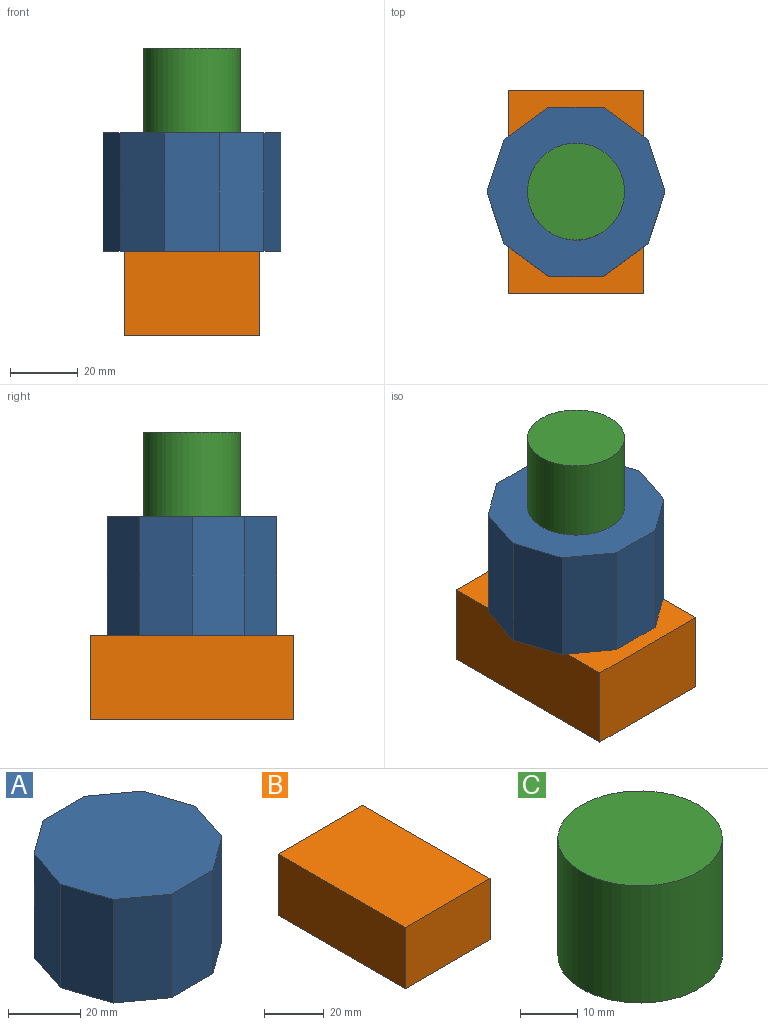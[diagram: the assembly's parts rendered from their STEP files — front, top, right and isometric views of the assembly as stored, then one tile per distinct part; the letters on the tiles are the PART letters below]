
ASSEMBLY  parts=3 mates=2
PART A: 12 faces, bbox 52.6x50x35 mm
  f0: plane 35x16.25mm, normal (0,1,0), area 568.6mm2, adj f1,f9,f10,f11
  f1: plane 35x13.14mm, normal (-0.59,0.81,0), area 568.6mm2, adj f0,f2,f10,f11
  f2: plane 35x15.45mm, normal (-0.95,0.31,0), area 568.6mm2, adj f1,f3,f10,f11
  f3: plane 35x15.45mm, normal (-0.95,-0.31,0), area 568.6mm2, adj f2,f4,f10,f11
  f4: plane 35x13.14mm, normal (-0.59,-0.81,0), area 568.6mm2, adj f3,f5,f10,f11
  f5: plane 35x16.25mm, normal (0,-1,0), area 568.6mm2, adj f4,f6,f10,f11
  f6: plane 35x13.14mm, normal (0.59,-0.81,0), area 568.6mm2, adj f5,f7,f10,f11
  f7: plane 35x15.45mm, normal (0.95,-0.31,0), area 568.6mm2, adj f6,f8,f10,f11
  f8: plane 35x15.45mm, normal (0.95,0.31,0), area 568.6mm2, adj f7,f9,f10,f11
  f9: plane 35x13.14mm, normal (0.59,0.81,0), area 568.6mm2, adj f0,f8,f10,f11
  f10: plane 52.57x50mm, normal (0,0,1), area 2030.7mm2, adj f0,f1,f2,f3,f4,f5,f6,f7
  f11: plane 52.57x50mm, normal (0,0,-1), area 2030.7mm2, adj f0,f1,f2,f3,f4,f5,f6,f7
PART B: 6 faces, bbox 40x60x25 mm
  f0: plane 60x25mm, normal (1,0,0), area 1500mm2, adj f1,f3,f4,f5
  f1: plane 40x25mm, normal (0,1,0), area 1000mm2, adj f0,f2,f4,f5
  f2: plane 60x25mm, normal (-1,0,0), area 1500mm2, adj f1,f3,f4,f5
  f3: plane 40x25mm, normal (0,-1,0), area 1000mm2, adj f0,f2,f4,f5
  f4: plane 60x40mm, normal (0,0,1), area 2400mm2, adj f0,f1,f2,f3
  f5: plane 60x40mm, normal (0,0,-1), area 2400mm2, adj f0,f1,f2,f3
PART C: 3 faces, bbox 28.7x28.7x25 mm
  f0: cylinder r=14.33mm len=28.66mm, axis (0,0,-1), area 2250.6mm2, adj f1,f2
  f1: plane 28.66x28.66mm, normal (0,0,1), area 644.9mm2, adj f0
  f2: plane 28.66x28.66mm, normal (0,0,-1), area 644.9mm2, adj f0
PLACE A t=(0,0,25)mm
PLACE B at identity fixed
PLACE C t=(0,0,60)mm
MATE fastened A.f10 <-> C.f0  axis (0,0,1) through (0,0,60)mm
MATE fastened B.f4 <-> A.f11  axis (0,0,1) through (0,0,25)mm
